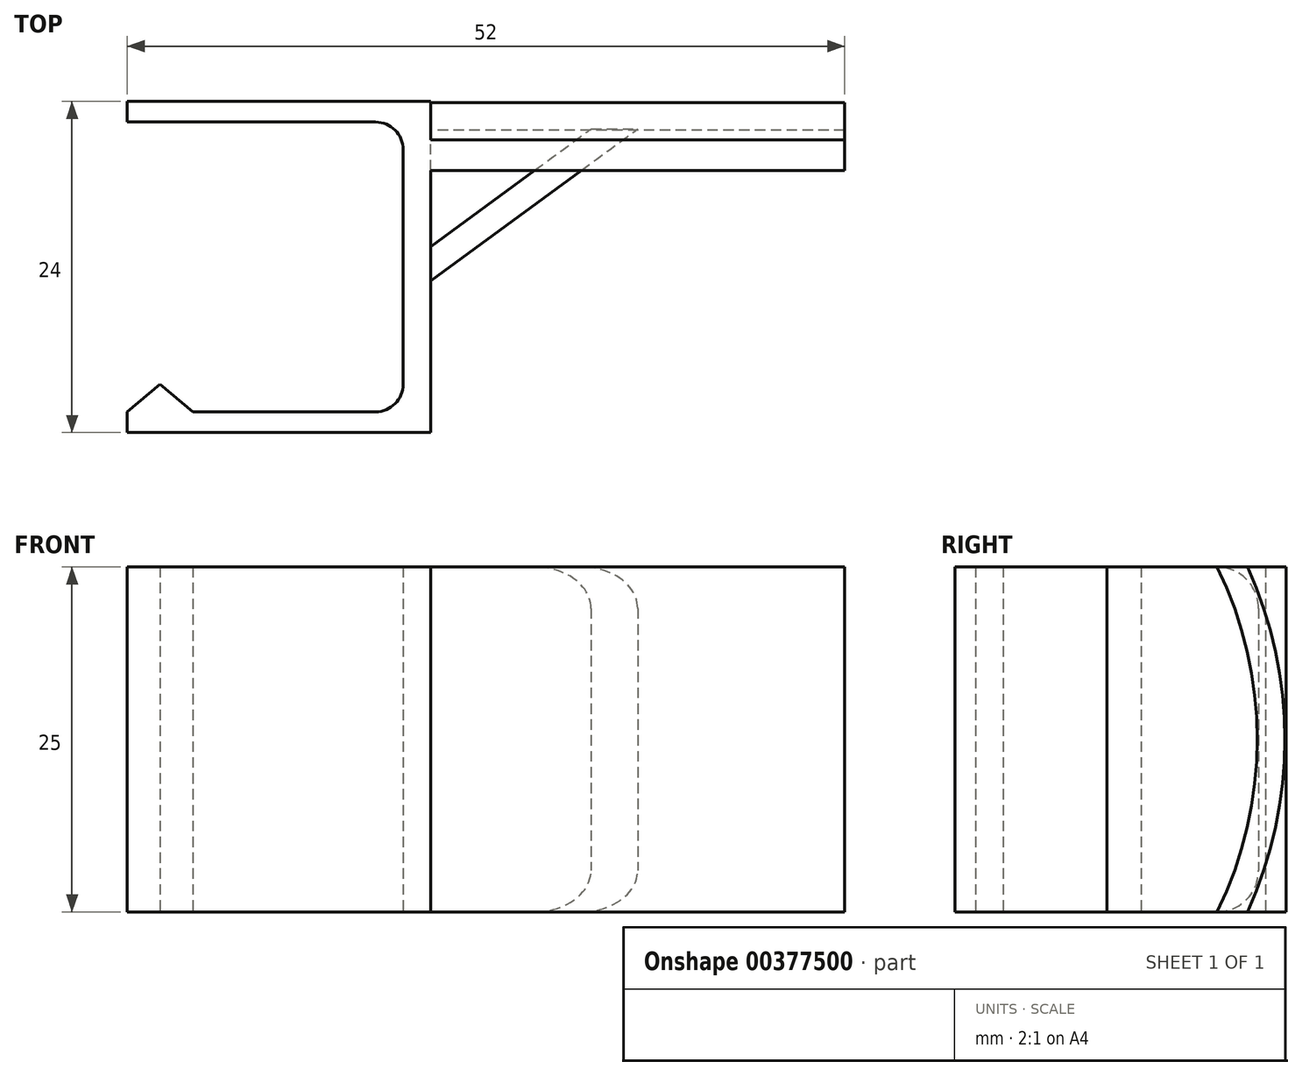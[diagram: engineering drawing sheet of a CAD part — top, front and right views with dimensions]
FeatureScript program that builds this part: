
annotation { "Feature Type Name" : "Feature", "Feature Type Description" : "" }
export const myFeature = defineFeature(function(context is Context, id is Id, definition is map)
    precondition{}
    {
        {
            var Q0;
            Q0=qCreatedBy(makeId("Top.planeOp"),FACE);
            var sketch = newSketch(context, id + "F0", { "sketchPlane" : qUnion([Q0])});
            skLineSegment(sketch, "E0.bottom", {"start": v(-22, 22.5) * mm, "end": v(26, 22.5) * mm});
            skLineSegment(sketch, "E0.top", {"start": v(-22, 21) * mm, "end": v(-4, 21) * mm});
            skLineSegment(sketch, "E0.left", {"start": v(-22, 22.5) * mm, "end": v(-22, 21) * mm});
            skLineSegment(sketch, "E1.top", {"start": v(3, 20.5) * mm, "end": v(30, 20.5) * mm});
            skLineSegment(sketch, "E1.right", {"start": v(30, 25.5) * mm, "end": v(30, 20.5) * mm});
            skLineSegment(sketch, "E2.top", {"start": v(0, -1.5) * mm, "end": v(-2, -1.5) * mm});
            skLineSegment(sketch, "E2.left", {"start": v(0, 17.5) * mm, "end": v(0, -1.5) * mm});
            skLineSegment(sketch, "E2.right", {"start": v(-2, 19) * mm, "end": v(-2, 2) * mm});
            skLineSegment(sketch, "E3.bottom", {"start": v(-2, -1.5) * mm, "end": v(-22, -1.5) * mm});
            skLineSegment(sketch, "E3.top", {"start": v(-4, 0) * mm, "end": v(-22, 0) * mm});
            skLineSegment(sketch, "E3.right", {"start": v(-22, -1.5) * mm, "end": v(-22, 0) * mm});
            skLineSegment(sketch, "E4", {"start": v(15, 20.5) * mm, "end": v(0, 9.5) * mm});
            skLineSegment(sketch, "E5", {"start": v(11.62, 20.5) * mm, "end": v(0, 11.98) * mm});
            skPoint(sketch, "E6.visualSharp", {"position": v(0, 20.5) * mm});
            skArc(sketch, "E6.filletArc", {"start": v(3, 20.5) * mm, "mid": v(0.88, 19.62) * mm, "end": v(0, 17.5) * mm});
            skPoint(sketch, "E7.visualSharp", {"position": v(-2, 21) * mm});
            skArc(sketch, "E7.filletArc", {"start": v(-2, 19) * mm, "mid": v(-2.59, 20.41) * mm, "end": v(-4, 21) * mm});
            skPoint(sketch, "E8.visualSharp", {"position": v(-2, 0) * mm});
            skArc(sketch, "E8.filletArc", {"start": v(-4, 0) * mm, "mid": v(-2.59, 0.59) * mm, "end": v(-2, 2) * mm});
            skLineSegment(sketch, "E9.top", {"start": v(30, 25.5) * mm, "end": v(29, 25.5) * mm});
            skLineSegment(sketch, "E9.right", {"start": v(29, 25.5) * mm, "end": v(29, 25.5) * mm});
            skArc(sketch, "E10.filletArc", {"start": v(26, 22.5) * mm, "mid": v(28.12, 23.38) * mm, "end": v(29, 25.5) * mm});
            skLineSegment(sketch, "E11", {"start": v(0, 17.5) * mm, "end": v(0, 22.5) * mm});
            skLineSegment(sketch, "E12", {"start": v(-22, 21) * mm, "end": v(-19.62, 19) * mm});
            skLineSegment(sketch, "E13", {"start": v(-19.62, 19) * mm, "end": v(-17.23, 21) * mm});
            skLineSegment(sketch, "E14", {"start": v(-2, 10.5) * mm, "end": v(-4.3, 10.5) * mm});
            skLineSegment(sketch, "E15.MirrorCS", {"start": v(-22, 0) * mm, "end": v(-19.62, 2) * mm});
            skLineSegment(sketch, "E16.MirrorCS", {"start": v(-19.62, 2) * mm, "end": v(-17.23, 0) * mm});
            skSolve(sketch);
        }
        {
            var Q0;
            Q0=makeQuery(id+"F0.imprint","IMPRINT",FACE,{"disambiguationData":[TD([[makeQuery(id+"F0.imprint","IMPRINT",EDGE,{"derivedFrom":sQuery(id+"F0.wireOp",EDGE,"E0.top")}),1.0]])]});
            var Q1;
            {var subQ0=sQuery(id+"F0.wireOp",EDGE,"E15.MirrorCS");Q1=makeQuery(id+"F0.imprint","IMPRINT",FACE,{"disambiguationData":[TD([[makeQuery(id+"F0.imprint","IMPRINT",EDGE,{"derivedFrom":subQ0}),-1.0]])]});}
            extrude(context, id + "F1", {"entities" : qUnion([Q0, Q1]), "depth" : 25 * mm});
        }
        {
            var Q0;
            Q0=makeQuery(id+"F1.opExtrude","SWEPT_FACE",FACE,{"disambiguationData":[OSD([sQuery(id+"F0.wireOp",EDGE,"E2.left"),sQuery(id+"F0.wireOp",EDGE,"E11")])]});
            var sketch = newSketch(context, id + "F2", { "sketchPlane" : qUnion([Q0])});
            skArc(sketch, "E17", {"start": v(17.5, 0) * mm, "mid": v(20.4, 12.5) * mm, "end": v(17.5, 25) * mm});
            skArc(sketch, "E18.0", {"start": v(19.71, 0) * mm, "mid": v(22.4, 12.5) * mm, "end": v(19.71, 25) * mm});
            skSolve(sketch);
        }
        {
            var Q0;
            {var subQ0=sQuery(id+"F2.wireOp",EDGE,"E17");Q0=makeQuery(id+"F2.imprint","IMPRINT",FACE,{"disambiguationData":[TD([[makeQuery(id+"F2.imprint","IMPRINT",EDGE,{"derivedFrom":subQ0}),-1.0]])]});}
            extrude(context, id + "F3", {"entities" : qUnion([Q0]), "operationType" : NewBodyOperationType.ADD, "depth" : 30 * mm});
        }
        {
            var Q0;
            {var subQ0=sQuery(id+"F0.wireOp",EDGE,"E4");Q0=makeQuery(id+"F0.imprint","IMPRINT",FACE,{"disambiguationData":[TD([[makeQuery(id+"F0.imprint","IMPRINT",EDGE,{"derivedFrom":subQ0}),-1.0]])]});}
            extrude(context, id + "F4", {"entities" : qUnion([Q0]), "depth" : 25 * mm});
        }
        {
            var Q0;
            Q0=makeQuery(id+"F4.opExtrude","CAP_EDGE",EDGE,{"disambiguationData":[OSD([sQuery(id+"F0.wireOp",EDGE,"E1.top")])],"isStart":false});
            var Q1;
            Q1=makeQuery(id+"F4.opExtrude","CAP_EDGE",EDGE,{"disambiguationData":[OSD([sQuery(id+"F0.wireOp",EDGE,"E1.top")])],"isStart":true});
            fillet(context, id + "F5", {"entities" : qUnion([Q0, Q1]), "radius" : 3 * mm, "tangentPropagation" : true, "allowEdgeOverflow" : false});
        }
    });
